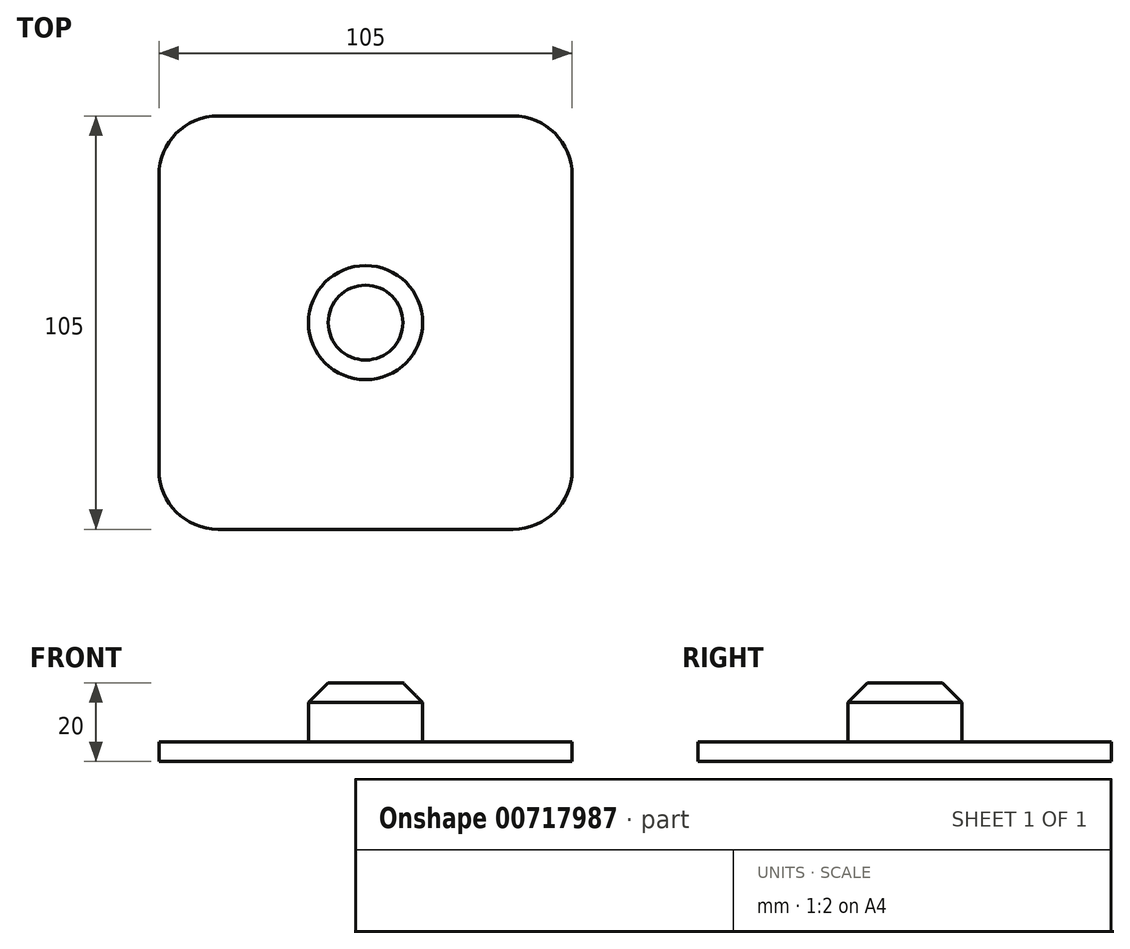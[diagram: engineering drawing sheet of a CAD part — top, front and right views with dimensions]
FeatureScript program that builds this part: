
annotation { "Feature Type Name" : "Feature", "Feature Type Description" : "" }
export const myFeature = defineFeature(function(context is Context, id is Id, definition is map)
    precondition{}
    {
        {
            var Q0;
            Q0=qCreatedBy(makeId("Top.planeOp"),FACE);
            var sketch = newSketch(context, id + "F0", { "sketchPlane" : qUnion([Q0])});
            skLineSegment(sketch, "E0.bottom", {"start": v(52.5, -52.5) * mm, "end": v(-52.5, -52.5) * mm});
            skLineSegment(sketch, "E0.top", {"start": v(52.5, 52.5) * mm, "end": v(-52.5, 52.5) * mm});
            skLineSegment(sketch, "E0.left", {"start": v(52.5, -52.5) * mm, "end": v(52.5, 52.5) * mm});
            skLineSegment(sketch, "E0.right", {"start": v(-52.5, -52.5) * mm, "end": v(-52.5, 52.5) * mm});
            skPoint(sketch, "E0.middle", {"position": v(0, 0) * mm});
            skCircle(sketch, "E1", {"center": v(0, 0) * mm, "radius": 14.5 * mm});
            skSolve(sketch);
        }
        {
            var Q0;
            Q0=makeQuery(id+"F0.imprint","IMPRINT",FACE,{"disambiguationData":[TD([[makeQuery(id+"F0.imprint","IMPRINT",EDGE,{"derivedFrom":sQuery(id+"F0.wireOp",EDGE,"E1")}),1.0]])]});
            extrude(context, id + "F1", {"entities" : qUnion([Q0]), "depth" : 20 * mm, "offsetDistance" : 25 * mm});
        }
        {
            var Q0;
            Q0=makeQuery(id+"F0.imprint","IMPRINT",FACE,{"disambiguationData":[TD([[makeQuery(id+"F0.imprint","IMPRINT",EDGE,{"derivedFrom":sQuery(id+"F0.wireOp",EDGE,"E0.bottom")}),-1.0]])]});
            extrude(context, id + "F2", {"entities" : qUnion([Q0]), "operationType" : NewBodyOperationType.ADD, "depth" : 5 * mm, "offsetDistance" : 25 * mm});
        }
        {
            var Q0;
            Q0=makeQuery(id+"F2.opExtrude","SWEPT_EDGE",EDGE,{"disambiguationData":[OSD([sQuery(id+"F0.wireOp",EDGE,"E0.bottom"),sQuery(id+"F0.wireOp",EDGE,"E0.left")])]});
            var Q1;
            Q1=makeQuery(id+"F2.opExtrude","SWEPT_EDGE",EDGE,{"disambiguationData":[OSD([sQuery(id+"F0.wireOp",EDGE,"E0.bottom"),sQuery(id+"F0.wireOp",EDGE,"E0.right")])]});
            var Q2;
            Q2=makeQuery(id+"F2.opExtrude","SWEPT_EDGE",EDGE,{"disambiguationData":[OSD([sQuery(id+"F0.wireOp",EDGE,"E0.top"),sQuery(id+"F0.wireOp",EDGE,"E0.right")])]});
            var Q3;
            Q3=makeQuery(id+"F2.opExtrude","SWEPT_EDGE",EDGE,{"disambiguationData":[OSD([sQuery(id+"F0.wireOp",EDGE,"E0.top"),sQuery(id+"F0.wireOp",EDGE,"E0.left")])]});
            fillet(context, id + "F3", {"entities" : qUnion([Q0, Q1, Q2, Q3]), "radius" : 15 * mm, "tangentPropagation" : true, "allowEdgeOverflow" : false});
        }
        {
            var Q0;
            Q0=makeQuery(id+"F1.opExtrude","CAP_EDGE",EDGE,{"disambiguationData":[OSD([sQuery(id+"F0.wireOp",EDGE,"E1")])],"isStart":false});
            chamfer(context, id + "F4", {"entities" : qUnion([Q0]), "width" : 5 * mm, "tangentPropagation" : true});
        }
    });
